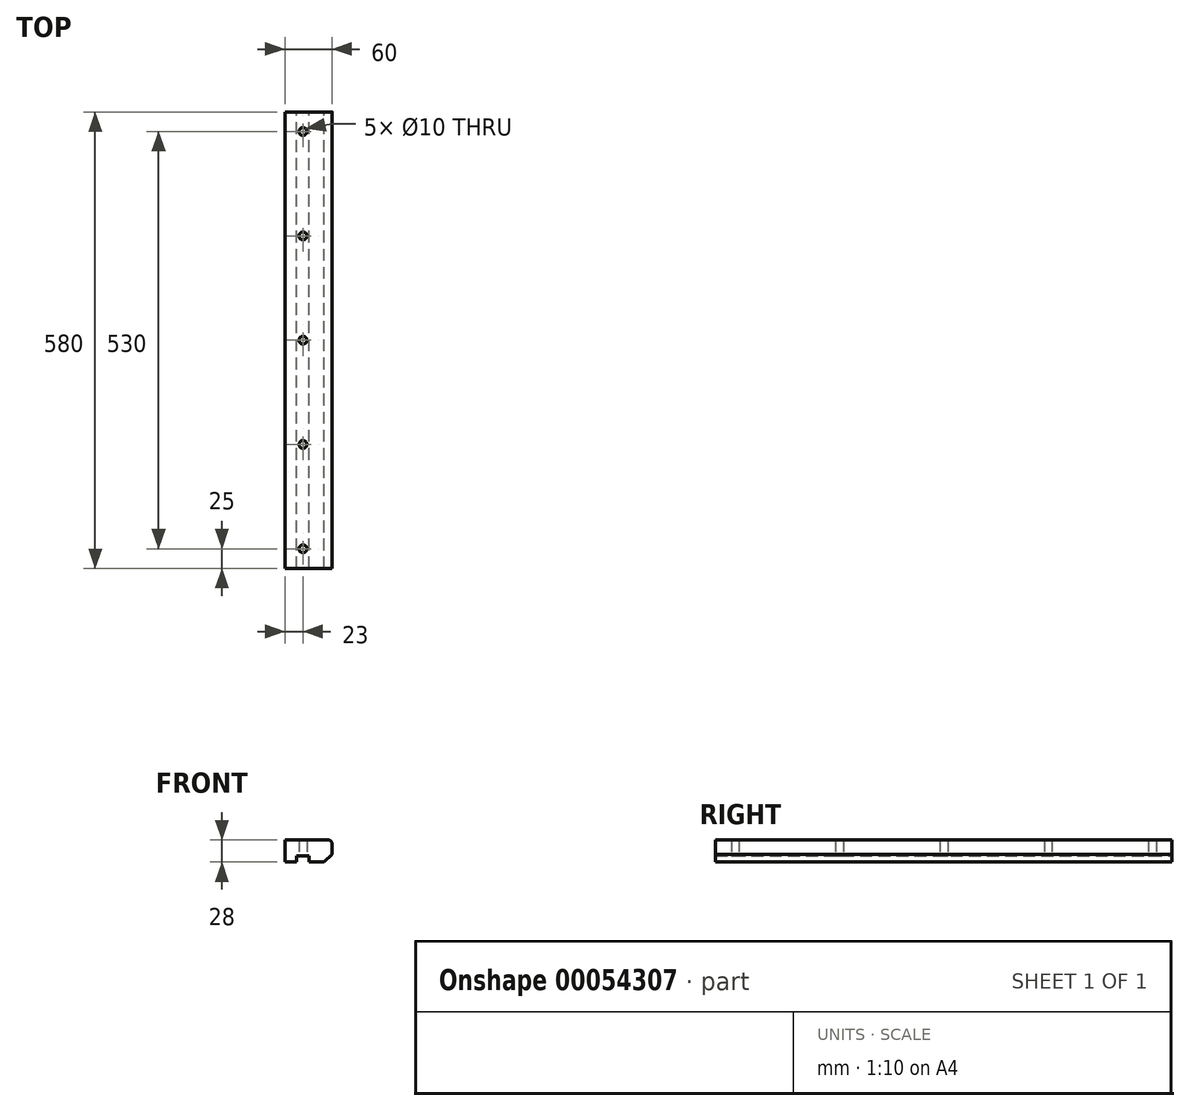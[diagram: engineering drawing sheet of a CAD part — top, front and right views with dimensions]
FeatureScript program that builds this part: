
annotation { "Feature Type Name" : "Feature", "Feature Type Description" : "" }
export const myFeature = defineFeature(function(context is Context, id is Id, definition is map)
    precondition{}
    {
        {
            var Q0;
            Q0=qCreatedBy(makeId("Front.planeOp"),FACE);
            var sketch = newSketch(context, id + "F0", { "sketchPlane" : qUnion([Q0])});
            skLineSegment(sketch, "E0", {"start": v(0, 0) * mm, "end": v(0, 28) * mm});
            skLineSegment(sketch, "E1", {"start": v(0, 28) * mm, "end": v(60, 28) * mm});
            skLineSegment(sketch, "E2", {"start": v(60, 28) * mm, "end": v(60, 10) * mm});
            skLineSegment(sketch, "E3", {"start": v(60, 10) * mm, "end": v(50, 0) * mm});
            skLineSegment(sketch, "E4", {"start": v(50, 0) * mm, "end": v(31, 0) * mm});
            skLineSegment(sketch, "E5", {"start": v(31, 0) * mm, "end": v(31, 8) * mm});
            skLineSegment(sketch, "E6", {"start": v(31, 8) * mm, "end": v(15, 8) * mm});
            skLineSegment(sketch, "E7", {"start": v(15, 8) * mm, "end": v(15, 0) * mm});
            skLineSegment(sketch, "E8", {"start": v(15, 0) * mm, "end": v(0, 0) * mm});
            skLineSegment(sketch, "E9", {"start": v(60, 10) * mm, "end": v(60, 0) * mm, "construction": true});
            skLineSegment(sketch, "E10", {"start": v(60, 0) * mm, "end": v(50, 0) * mm, "construction": true});
            skSolve(sketch);
        }
        {
            var Q0;
            Q0=makeQuery(id+"F0.imprint","IMPRINT",FACE,{"disambiguationData":[TD([[makeQuery(id+"F0.imprint","IMPRINT",EDGE,{"derivedFrom":sQuery(id+"F0.wireOp",EDGE,"E0")}),-1.0]])]});
            extrude(context, id + "F1", {"entities" : qUnion([Q0]), "depth" : 580 * mm});
        }
        {
            var Q0;
            Q0=makeQuery(id+"F1.opExtrude","SWEPT_FACE",FACE,{"disambiguationData":[OSD([sQuery(id+"F0.wireOp",EDGE,"E6")])]});
            var sketch = newSketch(context, id + "F2", { "sketchPlane" : qUnion([Q0])});
            skCircle(sketch, "E11", {"center": v(23, 25) * mm, "radius": 5 * mm});
            skPoint(sketch, "E11.centerSnap0", {"position": v(23, 0) * mm});
            skCircle(sketch, "E12", {"center": v(23, 157.5) * mm, "radius": 5 * mm});
            skCircle(sketch, "E13", {"center": v(23, 290) * mm, "radius": 5 * mm});
            skCircle(sketch, "E14", {"center": v(23, 422.5) * mm, "radius": 5 * mm});
            skCircle(sketch, "E15", {"center": v(23, 555) * mm, "radius": 5 * mm});
            skSolve(sketch);
        }
        {
            var Q0;
            Q0=makeQuery(id+"F2.imprint","IMPRINT",FACE,{"disambiguationData":[TD([[makeQuery(id+"F2.imprint","IMPRINT",EDGE,{"derivedFrom":sQuery(id+"F2.wireOp",EDGE,"E11")}),1.0]])]});
            var Q1;
            Q1=makeQuery(id+"F2.imprint","IMPRINT",FACE,{"disambiguationData":[TD([[makeQuery(id+"F2.imprint","IMPRINT",EDGE,{"derivedFrom":sQuery(id+"F2.wireOp",EDGE,"E12")}),1.0]])]});
            var Q2;
            Q2=makeQuery(id+"F2.imprint","IMPRINT",FACE,{"disambiguationData":[TD([[makeQuery(id+"F2.imprint","IMPRINT",EDGE,{"derivedFrom":sQuery(id+"F2.wireOp",EDGE,"E13")}),1.0]])]});
            var Q3;
            Q3=makeQuery(id+"F2.imprint","IMPRINT",FACE,{"disambiguationData":[TD([[makeQuery(id+"F2.imprint","IMPRINT",EDGE,{"derivedFrom":sQuery(id+"F2.wireOp",EDGE,"E14")}),1.0]])]});
            var Q4;
            Q4=makeQuery(id+"F2.imprint","IMPRINT",FACE,{"disambiguationData":[TD([[makeQuery(id+"F2.imprint","IMPRINT",EDGE,{"derivedFrom":sQuery(id+"F2.wireOp",EDGE,"E15")}),1.0]])]});
            var Q5;
            Q5=sQuery(id+"F2.wireOp",EDGE,"E11");
            var Q6;
            Q6=sQuery(id+"F2.wireOp",EDGE,"E12");
            var Q7;
            Q7=sQuery(id+"F2.wireOp",EDGE,"E13");
            var Q8;
            Q8=sQuery(id+"F2.wireOp",EDGE,"E14");
            var Q9;
            Q9=sQuery(id+"F2.wireOp",EDGE,"E15");
            extrude(context, id + "F3", {"entities" : qUnion([Q0, Q1, Q2, Q3, Q4]), "operationType" : NewBodyOperationType.REMOVE, "surfaceEntities" : qUnion([Q5, Q6, Q7, Q8, Q9]), "endBound" : BoundingType.THROUGH_ALL, "oppositeDirection" : true, "depth" : 25 * mm});
        }
        {
            var Q0;
            Q0=makeQuery(id+"F1.opExtrude","SWEPT_EDGE",EDGE,{"disambiguationData":[OSD([sQuery(id+"F0.wireOp",EDGE,"E1"),sQuery(id+"F0.wireOp",EDGE,"E2")])]});
            fillet(context, id + "F4", {"entities" : qUnion([Q0]), "radius" : 5 * mm, "tangentPropagation" : true, "allowEdgeOverflow" : false});
        }
    });
